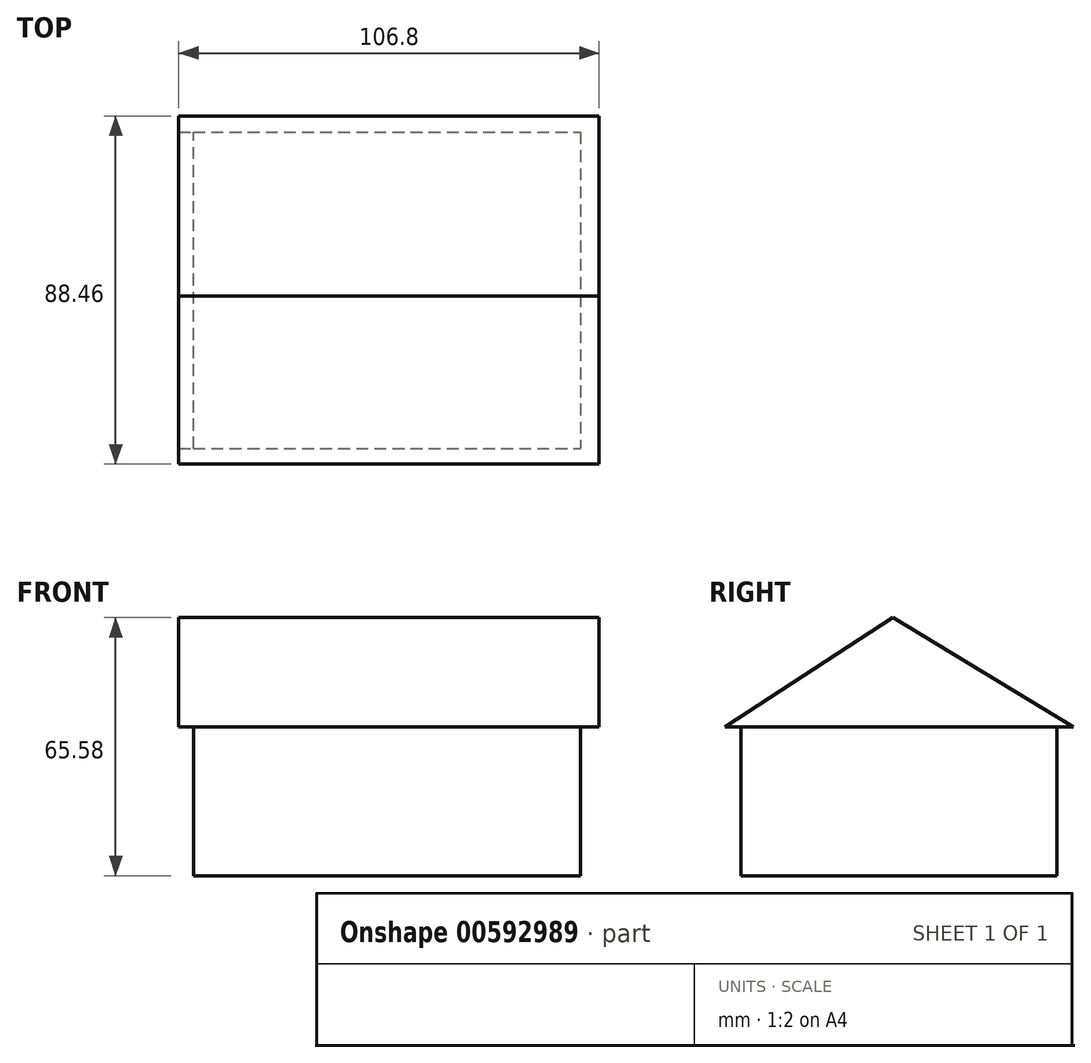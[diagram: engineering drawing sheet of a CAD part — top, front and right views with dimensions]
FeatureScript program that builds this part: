
annotation { "Feature Type Name" : "Feature", "Feature Type Description" : "" }
export const myFeature = defineFeature(function(context is Context, id is Id, definition is map)
    precondition{}
    {
        {
            var Q0;
            Q0=qCreatedBy(makeId("Right.planeOp"),FACE);
            var sketch = newSketch(context, id + "F0", { "sketchPlane" : qUnion([Q0])});
            skLineSegment(sketch, "E0.bottom", {"start": v(0, -18.98) * mm, "end": v(80.37, -18.98) * mm});
            skLineSegment(sketch, "E0.top", {"start": v(0, 19.09) * mm, "end": v(80.37, 19.09) * mm});
            skLineSegment(sketch, "E0.left", {"start": v(0, -18.98) * mm, "end": v(0, 19.09) * mm});
            skLineSegment(sketch, "E0.right", {"start": v(80.37, -18.98) * mm, "end": v(80.37, 19.09) * mm});
            skSolve(sketch);
        }
        {
            var Q0;
            Q0=makeQuery(id+"F0.imprint","IMPRINT",FACE,{"disambiguationData":[TD([[makeQuery(id+"F0.imprint","IMPRINT",EDGE,{"derivedFrom":sQuery(id+"F0.wireOp",EDGE,"E0.bottom")}),1.0]])]});
            extrude(context, id + "F1", {"entities" : qUnion([Q0]), "oppositeDirection" : true, "depth" : 49.2 * mm, "offsetDistance" : 25 * mm});
        }
        {
            var Q0;
            Q0=makeQuery(id+"F1.opExtrude","CAP_FACE",FACE,{"disambiguationData":[OSD([sQuery(id+"F0.wireOp",EDGE,"E0.bottom"),sQuery(id+"F0.wireOp",EDGE,"E0.top"),sQuery(id+"F0.wireOp",EDGE,"E0.left"),sQuery(id+"F0.wireOp",EDGE,"E0.right")])],"isStart":true});
            extrude(context, id + "F2", {"entities" : qUnion([Q0]), "operationType" : NewBodyOperationType.ADD, "depth" : 49.2 * mm, "offsetDistance" : 25 * mm});
        }
        {
            var Q0;
            Q0=qCreatedBy(makeId("Right.planeOp"),FACE);
            var sketch = newSketch(context, id + "F3", { "sketchPlane" : qUnion([Q0])});
            skLineSegment(sketch, "E1", {"start": v(-3.95, 18.8) * mm, "end": v(84.5, 18.8) * mm});
            skLineSegment(sketch, "E2", {"start": v(-3.95, 18.8) * mm, "end": v(38.7, 46.6) * mm});
            skLineSegment(sketch, "E3", {"start": v(38.7, 46.6) * mm, "end": v(84.5, 18.8) * mm});
            skSolve(sketch);
        }
        {
            var Q0;
            Q0=qSketchRegion(id+"F3",true);
            extrude(context, id + "F4", {"entities" : qUnion([Q0]), "operationType" : NewBodyOperationType.ADD, "depth" : 53.9 * mm, "offsetDistance" : 25 * mm});
        }
        {
            var Q0;
            Q0=makeQuery(id+"F4.opExtrude","CAP_FACE",FACE,{"disambiguationData":[OSD([sQuery(id+"F3.wireOp",EDGE,"E1"),sQuery(id+"F3.wireOp",EDGE,"E2"),sQuery(id+"F3.wireOp",EDGE,"E3")])],"isStart":true});
            extrude(context, id + "F5", {"entities" : qUnion([Q0]), "operationType" : NewBodyOperationType.ADD, "depth" : 52.9 * mm, "offsetDistance" : 25 * mm});
        }
    });
